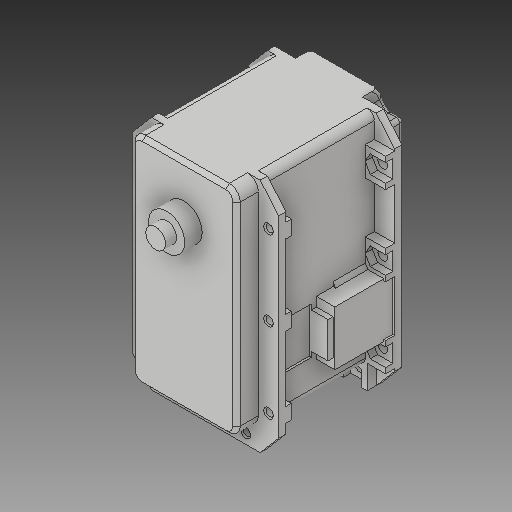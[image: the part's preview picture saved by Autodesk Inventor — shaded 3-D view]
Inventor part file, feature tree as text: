
AUTODESK INVENTOR PART (.ipt)
format: ipt  version: 2019 (Build 230136000, 136)  size: 523,264 bytes
history: native  units: in
note: dims shown in document units (in); Inventor stores cm internally (conversion verified against a paired STEP export)
features: extrude x1, sketch x1, projected_geometry x1, imported_body x1
ambient origin geometry x8: Origin, YZ Plane, XZ Plane, XY Plane, X Axis, Y Axis, Z Axis, Center Point
bodies: Solid1 (feature_tree)
feature tree (4):
  extrude  "Extrusion1"  [1 undecoded]
  sketch  "Sketch1"  dims[d0=0.1181in d1=0.0in]
  projected_geometry  "Projected Loop1"
  imported_body  "Base1"
note: 1 required parameter value undecoded (feature->parameter linkage not recoverable at this tier; creation-order binding heuristic only, values carry confidence <= 0.55)
